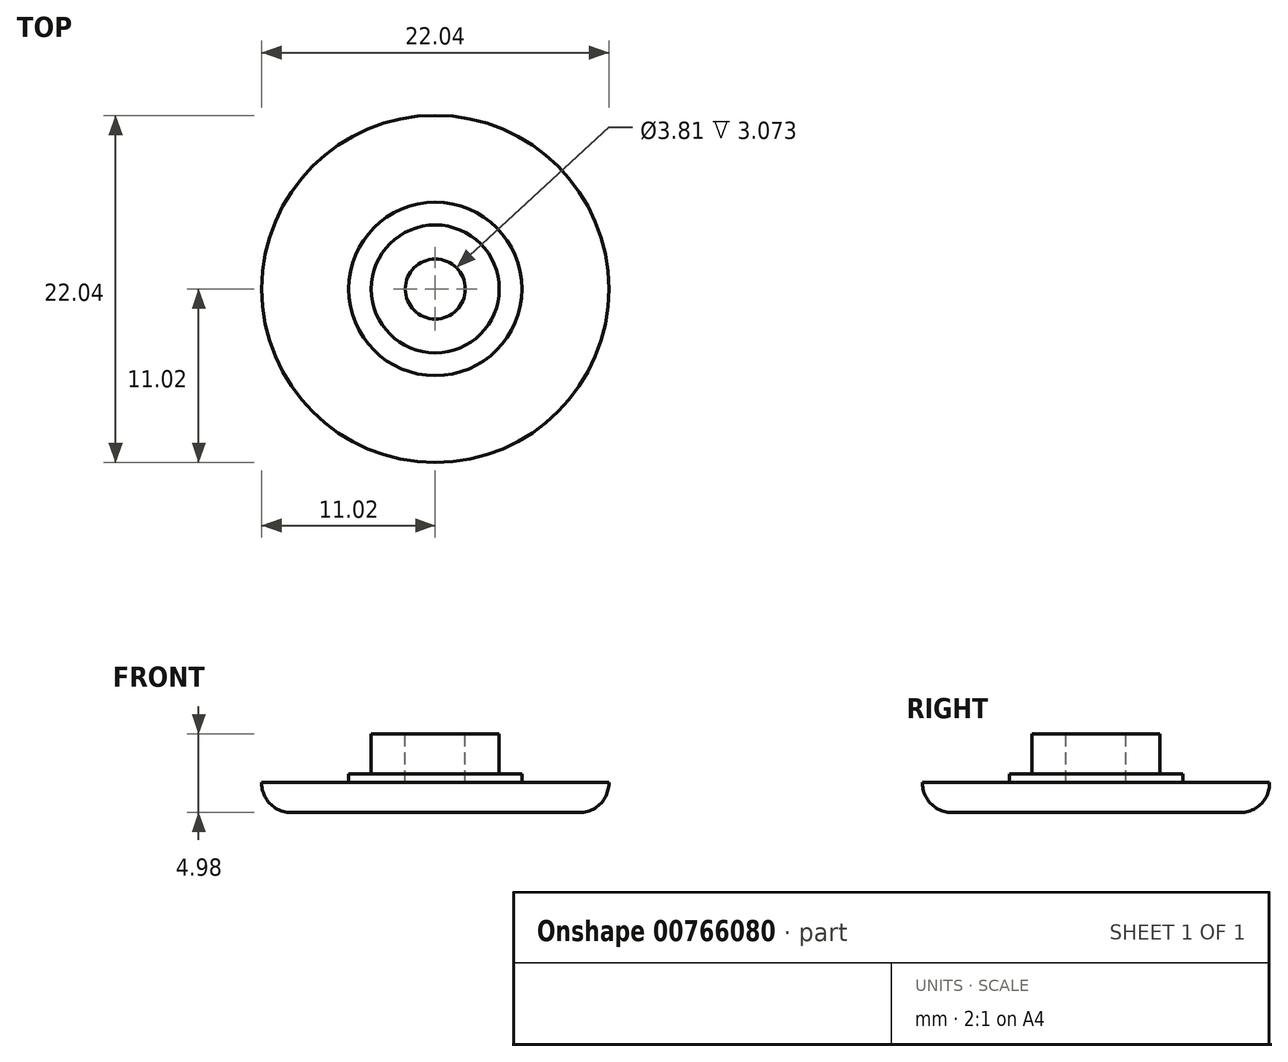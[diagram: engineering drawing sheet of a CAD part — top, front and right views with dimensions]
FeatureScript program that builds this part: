
annotation { "Feature Type Name" : "Feature", "Feature Type Description" : "" }
export const myFeature = defineFeature(function(context is Context, id is Id, definition is map)
    precondition{}
    {
        {
            var Q0;
            Q0=qCreatedBy(makeId("Top.planeOp"),FACE);
            var sketch = newSketch(context, id + "F0", { "sketchPlane" : qUnion([Q0])});
            skCircle(sketch, "E0", {"center": v(0, 0) * mm, "radius": 11.02 * mm});
            skSolve(sketch);
        }
        {
            var Q0;
            Q0=makeQuery(id+"F0.imprint","IMPRINT",FACE,{"disambiguationData":[TD([[makeQuery(id+"F0.imprint","IMPRINT",EDGE,{"derivedFrom":sQuery(id+"F0.wireOp",EDGE,"E0")}),1.0]])]});
            extrude(context, id + "F1", {"entities" : qUnion([Q0]), "depth" : 1.9 * mm, "offsetDistance" : 25.4 * mm});
        }
        {
            var Q0;
            Q0=makeQuery(id+"F1.opExtrude","CAP_FACE",FACE,{"disambiguationData":[OSD([sQuery(id+"F0.wireOp",EDGE,"E0")])],"isStart":false});
            var sketch = newSketch(context, id + "F2", { "sketchPlane" : qUnion([Q0])});
            skCircle(sketch, "E1", {"center": v(0, 0) * mm, "radius": 5.5 * mm});
            skSolve(sketch);
        }
        {
            var Q0;
            Q0=makeQuery(id+"F2.imprint","IMPRINT",FACE,{"disambiguationData":[TD([[makeQuery(id+"F2.imprint","IMPRINT",EDGE,{"derivedFrom":sQuery(id+"F2.wireOp",EDGE,"E1")}),1.0]])]});
            extrude(context, id + "F3", {"entities" : qUnion([Q0]), "operationType" : NewBodyOperationType.ADD, "depth" : 0.53 * mm, "offsetDistance" : 25.4 * mm});
        }
        {
            var Q0;
            Q0=makeQuery(id+"F3.opExtrude","CAP_FACE",FACE,{"disambiguationData":[OSD([sQuery(id+"F2.wireOp",EDGE,"E1")])],"isStart":false});
            var sketch = newSketch(context, id + "F4", { "sketchPlane" : qUnion([Q0])});
            skCircle(sketch, "E2", {"center": v(0, 0) * mm, "radius": 4.06 * mm});
            skSolve(sketch);
        }
        {
            var Q0;
            Q0=makeQuery(id+"F4.imprint","IMPRINT",FACE,{"disambiguationData":[TD([[makeQuery(id+"F4.imprint","IMPRINT",EDGE,{"derivedFrom":sQuery(id+"F4.wireOp",EDGE,"E2")}),1.0]])]});
            extrude(context, id + "F5", {"entities" : qUnion([Q0]), "operationType" : NewBodyOperationType.ADD, "depth" : 2.54 * mm, "offsetDistance" : 25.4 * mm});
        }
        {
            var Q0;
            Q0=makeQuery(id+"F5.opExtrude","CAP_FACE",FACE,{"disambiguationData":[OSD([sQuery(id+"F4.wireOp",EDGE,"E2")])],"isStart":false});
            var sketch = newSketch(context, id + "F6", { "sketchPlane" : qUnion([Q0])});
            skCircle(sketch, "E3", {"center": v(0, 0) * mm, "radius": 1.9 * mm});
            skSolve(sketch);
        }
        {
            var Q0;
            Q0=makeQuery(id+"F6.imprint","IMPRINT",FACE,{"disambiguationData":[TD([[makeQuery(id+"F6.imprint","IMPRINT",EDGE,{"derivedFrom":sQuery(id+"F6.wireOp",EDGE,"E3")}),1.0]])]});
            var Q1;
            Q1=makeQuery(id+"F1.opExtrude","CAP_FACE",FACE,{"disambiguationData":[OSD([sQuery(id+"F0.wireOp",EDGE,"E0")])],"isStart":false});
            extrude(context, id + "F7", {"entities" : qUnion([Q0]), "operationType" : NewBodyOperationType.REMOVE, "endBound" : BoundingType.UP_TO_SURFACE, "oppositeDirection" : true, "depth" : 25.4 * mm, "endBoundEntityFace" : qUnion([Q1]), "offsetDistance" : 25.4 * mm});
        }
        {
            var Q0;
            Q0=makeQuery(id+"F1.opExtrude","CAP_EDGE",EDGE,{"disambiguationData":[OSD([sQuery(id+"F0.wireOp",EDGE,"E0")])],"isStart":true});
            fillet(context, id + "F8", {"entities" : qUnion([Q0]), "radius" : 1.85 * mm, "tangentPropagation" : true, "allowEdgeOverflow" : false});
        }
    });
